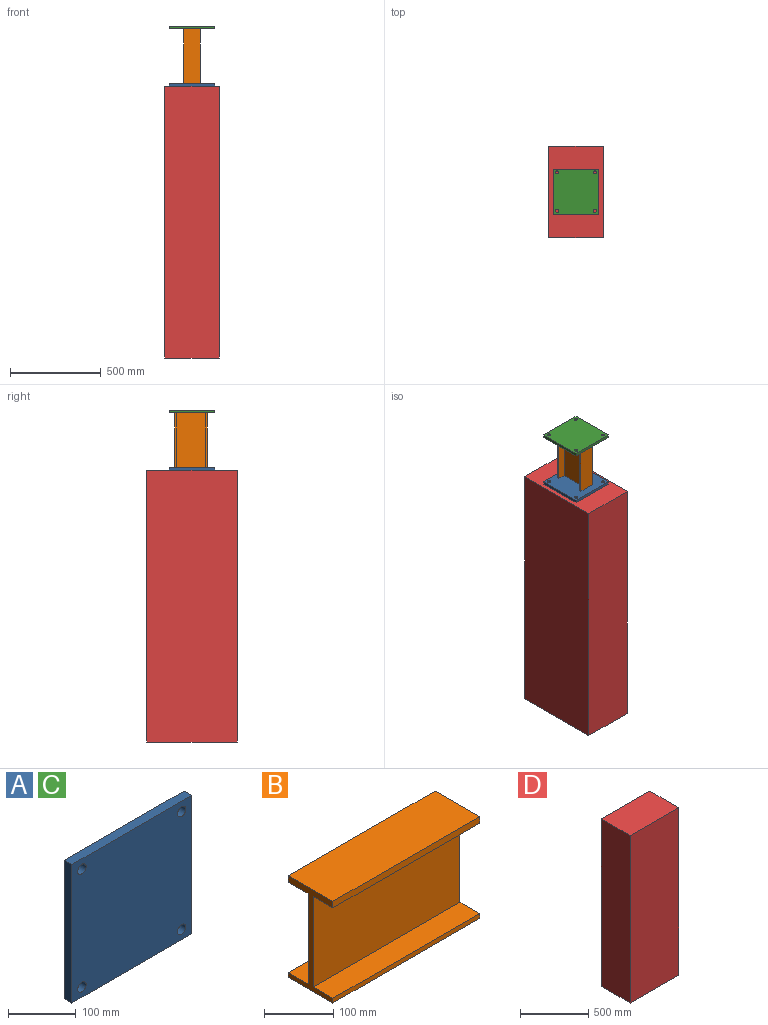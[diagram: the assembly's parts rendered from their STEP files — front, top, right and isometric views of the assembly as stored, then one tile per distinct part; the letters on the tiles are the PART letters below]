
ASSEMBLY  parts=4 mates=3
PART A: 10 faces, bbox 250x16x250 mm
  f0: plane 250x16mm, normal (0,0,1), area 4000mm2, adj f1,f3,f4,f5
  f1: plane 250x16mm, normal (-1,0,0), area 4000mm2, adj f0,f2,f4,f5
  f2: plane 250x16mm, normal (0,0,-1), area 4000mm2, adj f1,f3,f4,f5
  f3: plane 250x16mm, normal (1,0,0), area 4000mm2, adj f0,f2,f4,f5
  f4: plane 250x250mm, normal (0,-1,0), area 61537.9mm2, adj f0,f1,f2,f3,f6,f7,f8,f9
  f5: plane 250x250mm, normal (0,1,0), area 61537.9mm2, adj f0,f1,f2,f3,f6,f7,f8,f9
  f6: cylinder r=8.75mm len=17.5mm, axis (0,-1,0), area 879.6mm2, adj f4,f5
  f7: cylinder r=8.75mm len=17.5mm, axis (0,-1,0), area 879.6mm2, adj f4,f5
  f8: cylinder r=8.75mm len=17.5mm, axis (0,-1,0), area 879.6mm2, adj f4,f5
  f9: cylinder r=8.75mm len=17.5mm, axis (0,-1,0), area 879.6mm2, adj f4,f5
PART B: 14 faces, bbox 300x91x180 mm
  f0: plane 300x40.18mm, normal (0,0,-1), area 12052.9mm2, adj f1,f11,f12,f13
  f1: plane 300x11.61mm, normal (0,1,0), area 3481.4mm2, adj f0,f2,f12,f13
  f2: plane 300x91mm, normal (0,0,1), area 27300mm2, adj f1,f3,f12,f13
  f3: plane 300x11.61mm, normal (0,-1,0), area 3481.4mm2, adj f2,f4,f12,f13
  f4: plane 300x40.18mm, normal (0,0,-1), area 12052.9mm2, adj f3,f5,f12,f13
  f5: plane 300x160.1mm, normal (0,-1,0), area 48029.7mm2, adj f4,f6,f12,f13
  f6: plane 300x40.18mm, normal (0,0,1), area 12052.9mm2, adj f5,f7,f12,f13
  f7: plane 300x8.3mm, normal (0,-1,0), area 2488.9mm2, adj f6,f8,f12,f13
  f8: plane 300x91mm, normal (0,0,-1), area 27300mm2, adj f7,f9,f12,f13
  f9: plane 300x8.3mm, normal (0,1,0), area 2488.9mm2, adj f8,f10,f12,f13
  f10: plane 300x40.18mm, normal (0,0,1), area 12052.9mm2, adj f9,f11,f12,f13
  f11: plane 300x160.1mm, normal (0,1,0), area 48029.7mm2, adj f0,f10,f12,f13
  f12: plane 180x91mm, normal (1,0,0), area 3515.7mm2, adj f0,f1,f2,f3,f4,f5,f6,f7
  f13: plane 180x91mm, normal (-1,0,0), area 3515.7mm2, adj f0,f1,f2,f3,f4,f5,f6,f7
PART C: same geometry as A
PART D: 6 faces, bbox 500x300x1500 mm
  f0: plane 1500x300mm, normal (1,0,0), area 450000mm2, adj f1,f3,f4,f5
  f1: plane 1500x500mm, normal (0,1,0), area 750000mm2, adj f0,f2,f4,f5
  f2: plane 1500x300mm, normal (-1,0,0), area 450000mm2, adj f1,f3,f4,f5
  f3: plane 1500x500mm, normal (0,-1,0), area 750000mm2, adj f0,f2,f4,f5
  f4: plane 500x300mm, normal (0,0,-1), area 150000mm2, adj f0,f1,f2,f3
  f5: plane 500x300mm, normal (0,0,1), area 150000mm2, adj f0,f1,f2,f3
PLACE A rot(axis=(1,0,0),90deg) t=(-125,125,16)mm
PLACE B rot(axis=(0.58,0.58,-0.58),120deg) t=(0,2.35,316)mm
PLACE C rot(axis=(-1,0,0),90deg) t=(-125,-125,316)mm
PLACE D rot(axis=(0,0,1),90deg) t=(0,0,0)mm
MATE fastened B.f12 <-> A.f5  axis (0,0,-1) through (0,0,16)mm
MATE fastened C.f5 <-> B.f13  axis (0,0,-1) through (0,0,316)mm
MATE fastened A.f4 <-> D.f5  axis (0,0,-1) through (0,0,0)mm
